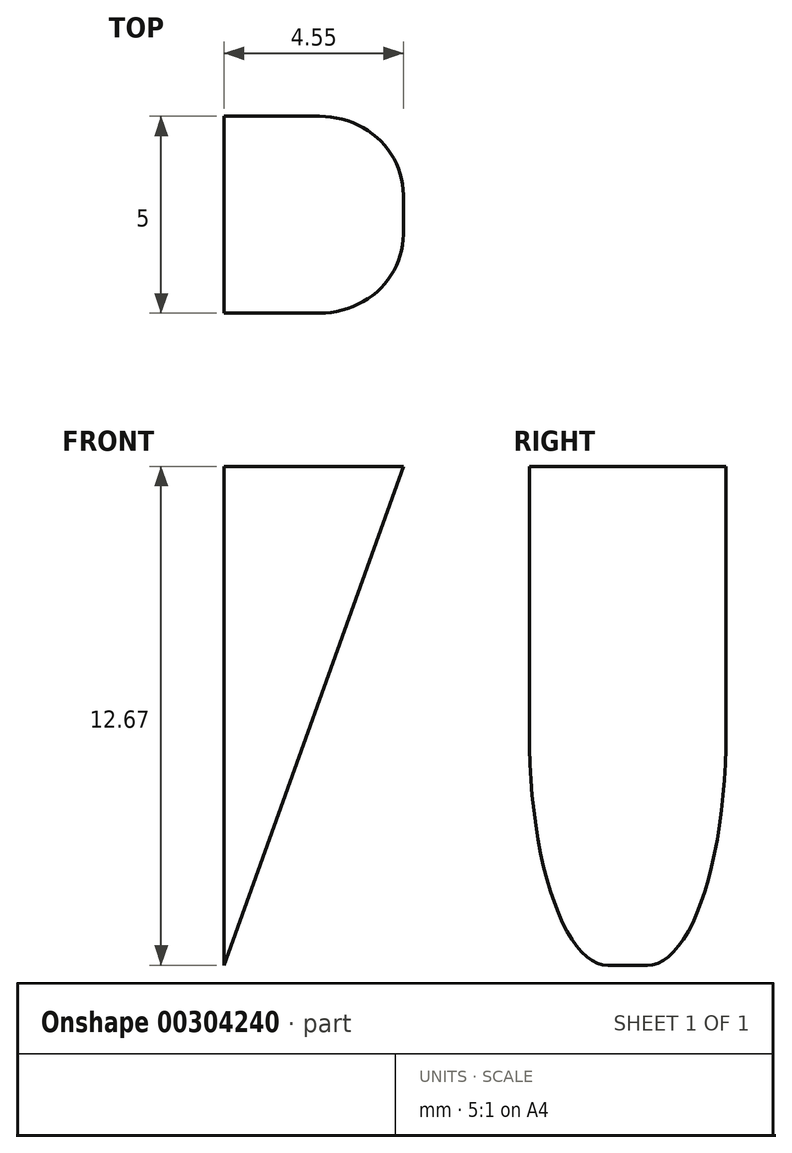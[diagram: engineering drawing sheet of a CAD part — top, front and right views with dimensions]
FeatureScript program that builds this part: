
annotation { "Feature Type Name" : "Feature", "Feature Type Description" : "" }
export const myFeature = defineFeature(function(context is Context, id is Id, definition is map)
    precondition{}
    {
        {
            var Q0;
            Q0=qCreatedBy(makeId("Front.planeOp"),FACE);
            var sketch = newSketch(context, id + "F0", { "sketchPlane" : qUnion([Q0])});
            skLineSegment(sketch, "E0", {"start": v(0, 0) * mm, "end": v(4.55, 0) * mm});
            skLineSegment(sketch, "E1", {"start": v(4.55, 0) * mm, "end": v(0, -12.67) * mm});
            skLineSegment(sketch, "E2", {"start": v(0, -12.67) * mm, "end": v(0, 0) * mm});
            skSolve(sketch);
        }
        {
            var Q0;
            Q0=makeQuery(id+"F0.imprint","IMPRINT",FACE,{"disambiguationData":[TD([[makeQuery(id+"F0.imprint","IMPRINT",EDGE,{"derivedFrom":sQuery(id+"F0.wireOp",EDGE,"E0")}),-1.0]])]});
            extrude(context, id + "F1", {"entities" : qUnion([Q0]), "endBound" : BoundingType.SYMMETRIC, "depth" : 5 * mm});
        }
        {
            var Q0;
            Q0=makeQuery(id+"F1.opExtrude","CAP_EDGE",EDGE,{"disambiguationData":[OSD([sQuery(id+"F0.wireOp",EDGE,"E1")])],"isStart":true});
            var Q1;
            Q1=makeQuery(id+"F1.opExtrude","CAP_EDGE",EDGE,{"disambiguationData":[OSD([sQuery(id+"F0.wireOp",EDGE,"E1")])],"isStart":false});
            fillet(context, id + "F2", {"entities" : qUnion([Q0, Q1]), "radius" : 2 * mm, "tangentPropagation" : true, "allowEdgeOverflow" : false});
        }
    });
